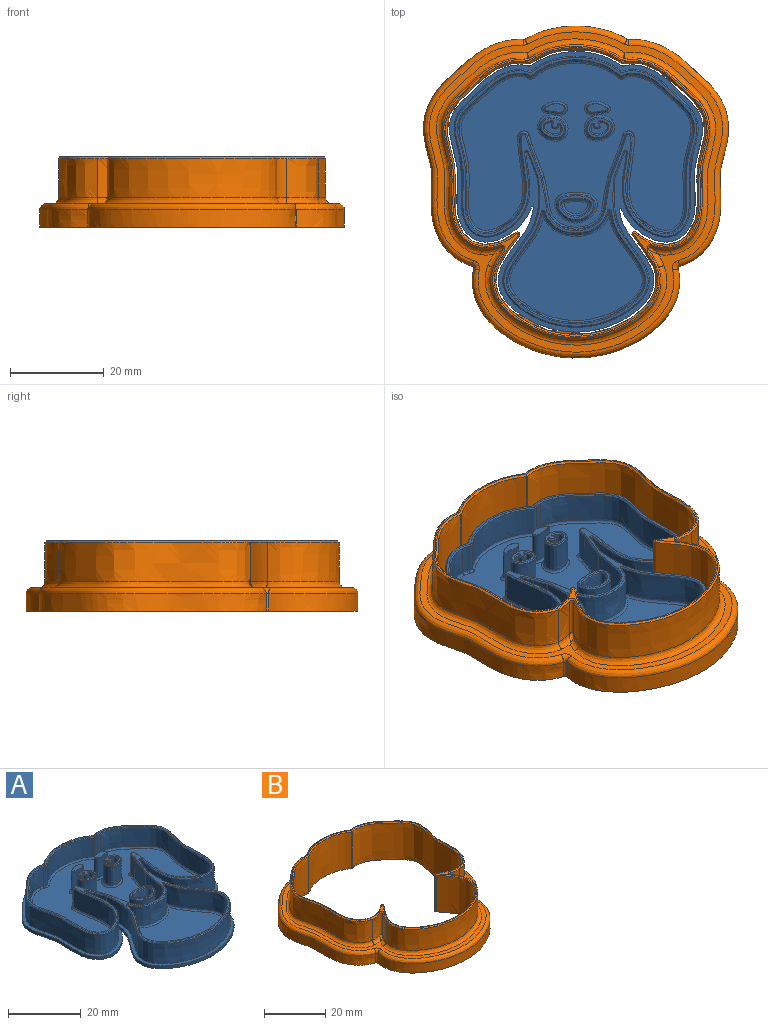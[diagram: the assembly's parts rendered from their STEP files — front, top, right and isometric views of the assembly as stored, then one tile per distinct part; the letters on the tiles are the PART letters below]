
ASSEMBLY  parts=2 mates=1
PART A: 147 faces, bbox 54.5x60.3x8.3 mm
  f0: plane 49.17x35.73mm, normal (0,0,1), area 1118mm2, adj f67,f68,f69,f70,f71,f72,f73,f74
  f1: plane 59.99x54.17mm, normal (0,0,1), area 259.7mm2, adj f2,f3,f4,f5,f20,f21,f22,f23
  f2: extruded ~37.82x17.38mm, area 63.9mm2, adj f1,f6,f57,f65
  f3: extruded ~19.16x2.96mm, area 20.4mm2, adj f1,f6,f65,f66
  f4: extruded ~37.76x17.54mm, area 64.3mm2, adj f1,f6,f58,f66
  f5: extruded ~33.25x26.68mm, area 78.1mm2, adj f1,f6,f57,f58
  f6: plane 59.99x54.17mm, normal (0,0,-1), area 2381.7mm2, adj f2,f3,f4,f5,f57,f58,f65,f66
  f7: extruded ~29.22x23.78mm, area 440.3mm2, adj f54,f55,f85,f133
  f8: extruded ~33.83x14.11mm, area 427.3mm2, adj f9,f59,f68,f115
  f9: extruded ~6.25x1.16mm, area 7.4mm2, adj f8,f10,f67,f116
  f10: extruded ~6.25x0.46mm, area 3.1mm2, adj f9,f61,f69,f118
  f11: extruded ~18.37x6.25mm, area 124.2mm2, adj f61,f62,f73,f122
  f12: extruded ~6.25x0.46mm, area 3.1mm2, adj f13,f62,f77,f126
  f13: extruded ~6.25x1.16mm, area 7.4mm2, adj f12,f14,f79,f128
  f14: extruded ~33.83x14.11mm, area 427.3mm2, adj f13,f64,f81,f130
  f15: extruded ~6.25x1.84mm, area 12mm2, adj f16,f64,f80,f127
  f16: extruded ~7.02x6.25mm, area 46.9mm2, adj f15,f17,f78,f125
  f17: extruded ~14.57x11.1mm, area 187.2mm2, adj f16,f18,f76,f123
  f18: extruded ~7.02x6.25mm, area 46.9mm2, adj f17,f19,f74,f121
  f19: extruded ~6.25x1.84mm, area 12mm2, adj f18,f59,f72,f119
  f20: extruded ~6.75x0.7mm, area 4.9mm2, adj f1,f21,f60,f106
  f21: extruded ~35.76x16.11mm, area 476.3mm2, adj f1,f20,f53,f104
  f22: extruded ~6.75x2.42mm, area 17.6mm2, adj f1,f23,f53,f100
  f23: extruded ~6.75x3.13mm, area 22.5mm2, adj f1,f22,f24,f99
  f24: extruded ~31.88x31.3mm, area 595mm2, adj f1,f23,f25,f101
  f25: extruded ~6.75x3.1mm, area 22.3mm2, adj f1,f24,f26,f103
  f26: extruded ~6.75x2.43mm, area 17.6mm2, adj f1,f25,f56,f105
  f27: extruded ~35.76x16.11mm, area 476.4mm2, adj f1,f28,f56,f109
  f28: extruded ~6.75x0.7mm, area 4.9mm2, adj f1,f27,f63,f111
  f29: extruded ~6.75x0.51mm, area 4.3mm2, adj f1,f30,f63,f114
  f30: extruded ~17.72x6.75mm, area 127mm2, adj f1,f29,f31,f112
  f31: extruded ~6.75x0.51mm, area 4.3mm2, adj f1,f30,f60,f110
  f32: extruded ~13.77x6.25mm, area 113mm2, adj f54,f55,f84,f132
  f33: plane 57.77x52.07mm, normal (0,0,1), area 101.2mm2, adj f99,f100,f101,f102,f103,f104,f105,f106
  f34: plane 28.32x22.06mm, normal (0,0,1), area 426.1mm2, adj f84,f85
  f35: extruded ~6.25x6.1mm, area 98.1mm2, adj f92,f98
  f36: extruded ~8.06x6.25mm, area 137.2mm2, adj f91,f97
  f37: plane 8.01x5.38mm, normal (0,0,1), area 9.6mm2, adj f97,f98
  f38: plane 5.13x2.56mm, normal (0,0,1), area 10mm2, adj f92
  f39: cylinder r=0.8mm len=6.75mm, axis (0,0,-1), area 21.2mm2, adj f43,f93,f94,f136
  f40: extruded ~6.75x3.54mm, area 54.2mm2, adj f43,f93,f94,f137
  f41: extruded ~6.25x5.54mm, area 100.7mm2, adj f90,f139
  f42: plane 5.29x4.35mm, normal (0,0,1), area 7.9mm2, adj f135,f136,f137,f138,f139
  f43: plane 3.66x2.67mm, normal (0,0,1), area 5.4mm2, adj f39,f40,f93,f94
  f44: extruded ~6.75x3.54mm, area 54.2mm2, adj f48,f95,f96,f142
  f45: extruded ~6.25x5.54mm, area 100.7mm2, adj f89,f144
  f46: cylinder r=0.8mm len=6.75mm, axis (0,0,-1), area 21.2mm2, adj f48,f95,f96,f141
  f47: plane 5.3x4.36mm, normal (0,0,1), area 8mm2, adj f140,f141,f142,f143,f144
  f48: plane 3.66x2.67mm, normal (0,0,1), area 5.4mm2, adj f44,f46,f95,f96
  f49: extruded ~6.4x4.57mm, area 68.2mm2, adj f88,f145
  f50: plane 4.48x1.88mm, normal (0,0,1), area 5.7mm2, adj f145
  f51: extruded ~6.4x4.57mm, area 68.2mm2, adj f87,f146
  f52: plane 4.49x1.9mm, normal (0,0,1), area 5.6mm2, adj f146
  f53: cylinder r=0.2mm len=6.75mm, axis (0,0,-1), area 3.9mm2, adj f1,f21,f22,f102
  f54: cylinder r=0.2mm len=6.25mm, axis (0,0,-1), area 3.4mm2, adj f7,f32,f86,f131
  f55: cylinder r=0.2mm len=6.25mm, axis (0,0,-1), area 3.4mm2, adj f7,f32,f83,f134
  f56: cylinder r=0.2mm len=6.75mm, axis (0,0,-1), area 3.9mm2, adj f1,f26,f27,f107
  f57: cylinder r=0.2mm len=1mm, axis (0,0,-1), area 0.6mm2, adj f1,f2,f5,f6
  f58: cylinder r=0.2mm len=1mm, axis (0,0,-1), area 0.6mm2, adj f1,f4,f5,f6
  f59: cylinder r=0.75mm len=6.25mm, axis (0,0,-1), area 13.4mm2, adj f8,f19,f70,f117
  f60: cylinder r=0.75mm len=6.75mm, axis (0,0,-1), area 5.2mm2, adj f1,f20,f31,f108
  f61: cylinder r=0.75mm len=6.25mm, axis (0,0,-1), area 5.8mm2, adj f10,f11,f71,f120
  f62: cylinder r=0.75mm len=6.25mm, axis (0,0,-1), area 5.8mm2, adj f11,f12,f75,f124
  f63: cylinder r=0.75mm len=6.75mm, axis (0,0,-1), area 5.2mm2, adj f1,f28,f29,f113
  f64: cylinder r=0.75mm len=6.25mm, axis (0,0,-1), area 13.5mm2, adj f14,f15,f82,f129
  f65: cylinder r=0.75mm len=1mm, axis (0,0,-1), area 0.7mm2, adj f1,f2,f3,f6
  f66: cylinder r=0.75mm len=1mm, axis (0,0,-1), area 0.7mm2, adj f1,f3,f4,f6
  f67: bspline ~1.47x0.77mm, area 0.9mm2, adj f0,f9,f68,f69
  f68: bspline ~33.87x24.37mm, area 53.1mm2, adj f0,f8,f67,f70
  f69: bspline ~0.91x0.78mm, area 0.4mm2, adj f0,f10,f67,f71
  f70: torus R=1.25mm, axis (0,0,1), area 2.1mm2, adj f0,f59,f68,f72
  f71: torus R=1.25mm, axis (0,0,1), area 0.9mm2, adj f0,f61,f69,f73
  f72: bspline ~3.24x1.36mm, area 1.5mm2, adj f0,f19,f70,f74
  f73: bspline ~19x4.03mm, area 15.4mm2, adj f0,f11,f71,f75
  f74: bspline ~10.3x4.11mm, area 5.9mm2, adj f0,f18,f72,f76
  f75: torus R=1.25mm, axis (0,0,1), area 0.9mm2, adj f0,f62,f73,f77
  f76: bspline ~17.48x16.85mm, area 23.1mm2, adj f0,f17,f74,f78
  f77: bspline ~0.89x0.74mm, area 0.4mm2, adj f0,f12,f75,f79
  f78: bspline ~10.33x4.12mm, area 5.9mm2, adj f0,f16,f76,f80
  f79: bspline ~1.64x0.78mm, area 0.9mm2, adj f0,f13,f77,f81
  f80: bspline ~3.26x1.37mm, area 1.5mm2, adj f0,f15,f78,f82
  f81: bspline ~33.88x14.21mm, area 53.1mm2, adj f0,f14,f79,f82
  f82: torus R=1.25mm, axis (0,0,1), area 2.1mm2, adj f0,f64,f80,f81
  f83: bspline ~2.25x0.67mm, area 0.3mm2, adj f55,f84,f85
  f84: bspline ~15.03x5.89mm, area 13.7mm2, adj f32,f34,f83,f86
  f85: bspline ~29.33x24.78mm, area 53.9mm2, adj f7,f34,f83,f86
  f86: bspline ~1.96x0.65mm, area 0.3mm2, adj f54,f84,f85
  f87: bspline ~5.58x2.99mm, area 9.3mm2, adj f0,f51
  f88: bspline ~5.58x2.99mm, area 9.3mm2, adj f0,f49
  f89: bspline ~6.55x5.6mm, area 13.6mm2, adj f0,f45
  f90: bspline ~6.55x5.59mm, area 13.5mm2, adj f0,f41
  f91: bspline ~9.13x6.56mm, area 18.2mm2, adj f0,f36
  f92: bspline ~6.13x3.56mm, area 11.3mm2, adj f35,f38
  f93: cylinder r=0.1mm len=6.75mm, axis (0,0,-1), area 1.7mm2, adj f39,f40,f43,f135
  f94: cylinder r=0.1mm len=6.75mm, axis (0,0,-1), area 1.6mm2, adj f39,f40,f43,f138
  f95: cylinder r=0.1mm len=6.75mm, axis (0,0,-1), area 1.6mm2, adj f44,f46,f48,f140
  f96: cylinder r=0.1mm len=6.75mm, axis (0,0,-1), area 1.7mm2, adj f44,f46,f48,f143
  f97: bspline ~8.11x5.55mm, area 7.5mm2, adj f36,f37
  f98: bspline ~6.62x4.05mm, area 5.8mm2, adj f35,f37
  f99: bspline ~3.41x1.44mm, area 1.2mm2, adj f23,f33,f100,f101
  f100: bspline ~2.51x1.19mm, area 0.9mm2, adj f22,f33,f99,f102
  f101: bspline ~36.19x31.37mm, area 31mm2, adj f24,f33,f99,f103
  f102: cone r=0.45mm half-angle=45deg, axis (0,0,1), area 0.3mm2, adj f33,f53,f100,f104
  f103: bspline ~3.39x1.44mm, area 1.2mm2, adj f25,f33,f101,f105
  f104: bspline ~35.95x16.31mm, area 24.7mm2, adj f21,f33,f102,f106
  f105: bspline ~2.52x1.19mm, area 0.9mm2, adj f26,f33,f103,f107
  f106: bspline ~0.75x0.43mm, area 0.3mm2, adj f20,f33,f104,f108
  f107: cone r=0.45mm half-angle=45deg, axis (0,0,1), area 0.3mm2, adj f33,f56,f105,f109
  f108: cone r=1mm half-angle=45deg, axis (0,0,1), area 0.3mm2, adj f33,f60,f106,f110
  f109: bspline ~35.96x16.32mm, area 24.5mm2, adj f27,f33,f107,f111
  f110: bspline ~0.65x0.58mm, area 0.2mm2, adj f31,f33,f108,f112
  f111: bspline ~0.75x0.43mm, area 0.3mm2, adj f28,f33,f109,f113
  f112: bspline ~17.72x2.88mm, area 6.6mm2, adj f30,f33,f110,f114
  f113: cone r=1mm half-angle=45deg, axis (0,0,1), area 0.3mm2, adj f33,f63,f111,f114
  f114: bspline ~0.65x0.58mm, area 0.2mm2, adj f29,f33,f112,f113
  f115: bspline ~34.49x14.72mm, area 24.5mm2, adj f8,f33,f116,f117
  f116: bspline ~1.24x0.47mm, area 0.4mm2, adj f9,f33,f115,f118
  f117: cone r=0.5mm half-angle=45deg, axis (0,0,-1), area 0.6mm2, adj f33,f59,f115,f119
  f118: bspline ~0.58x0.44mm, area 0.2mm2, adj f10,f33,f116,f120
  f119: bspline ~1.92x0.78mm, area 0.7mm2, adj f19,f33,f117,f121
  f120: cone r=0.5mm half-angle=45deg, axis (0,0,-1), area 0.3mm2, adj f33,f61,f118,f122
  f121: bspline ~7.09x2.87mm, area 2.6mm2, adj f18,f33,f119,f123
  f122: bspline ~18.7x3.45mm, area 7.1mm2, adj f11,f33,f120,f124
  f123: bspline ~15.05x11.35mm, area 10.7mm2, adj f17,f33,f121,f125
  f124: cone r=0.5mm half-angle=45deg, axis (0,0,-1), area 0.3mm2, adj f33,f62,f122,f126
  f125: bspline ~7.09x2.87mm, area 2.6mm2, adj f16,f33,f123,f127
  f126: bspline ~0.58x0.44mm, area 0.2mm2, adj f12,f33,f124,f128
  f127: bspline ~1.92x0.78mm, area 0.7mm2, adj f15,f33,f125,f129
  f128: bspline ~1.24x0.47mm, area 0.4mm2, adj f13,f33,f126,f130
  f129: cone r=0.5mm half-angle=45deg, axis (0,0,-1), area 0.6mm2, adj f33,f64,f127,f130
  f130: bspline ~34.46x14.72mm, area 24.4mm2, adj f14,f33,f128,f129
  f131: cone r=0.45mm half-angle=45deg, axis (0,0,1), area 0.3mm2, adj f33,f54,f132,f133
  f132: bspline ~13.77x4.92mm, area 6.3mm2, adj f32,f33,f131,f134
  f133: bspline ~29.91x24.07mm, area 25.1mm2, adj f7,f33,f131,f134
  f134: cone r=0.45mm half-angle=45deg, axis (0,0,1), area 0.3mm2, adj f33,f55,f132,f133
  f135: cone r=0.35mm half-angle=45deg, axis (0,0,1), area 0.2mm2, adj f42,f93,f136,f137
  f136: cone r=0.55mm half-angle=45deg, axis (0,0,-1), area 0.9mm2, adj f39,f42,f135,f138
  f137: bspline ~4.09x3.1mm, area 3.1mm2, adj f40,f42,f135,f138
  f138: cone r=0.35mm half-angle=45deg, axis (0,0,1), area 0.2mm2, adj f42,f94,f136,f137
  f139: bspline ~5.58x4.64mm, area 5.4mm2, adj f41,f42
  f140: cone r=0.35mm half-angle=45deg, axis (0,0,1), area 0.2mm2, adj f47,f95,f141,f142
  f141: cone r=0.55mm half-angle=45deg, axis (0,0,-1), area 0.9mm2, adj f46,f47,f140,f143
  f142: bspline ~4.09x3.1mm, area 3.1mm2, adj f44,f47,f140,f143
  f143: cone r=0.35mm half-angle=45deg, axis (0,0,1), area 0.2mm2, adj f47,f96,f141,f142
  f144: bspline ~5.54x4.59mm, area 5.4mm2, adj f45,f47
  f145: bspline ~4.59x1.99mm, area 1.5mm2, adj f49,f50
  f146: bspline ~4.59x2.01mm, area 1.5mm2, adj f51,f52
PART B: 85 faces, bbox 65.6x71.4x15.5 mm
  f0: extruded ~40.8x18.2mm, area 461.4mm2, adj f1,f33,f56,f83
  f1: extruded ~8.4x3.99mm, area 34.1mm2, adj f0,f37,f58,f81
  f2: extruded ~8.4x3.68mm, area 35.4mm2, adj f3,f37,f62,f77
  f3: extruded ~36.25x15.36mm, area 453.4mm2, adj f2,f4,f64,f75
  f4: extruded ~8.4x3.67mm, area 35.2mm2, adj f3,f35,f63,f73
  f5: extruded ~8.4x3.98mm, area 33.9mm2, adj f6,f35,f59,f76
  f6: extruded ~40.8x18.2mm, area 461.2mm2, adj f5,f34,f57,f78
  f7: extruded ~20.01x8.4mm, area 177.7mm2, adj f33,f34,f53,f82
  f8: extruded ~14.65x6.78mm, area 108.4mm2, adj f9,f21,f23,f40
  f9: extruded ~38.85x17.49mm, area 771.2mm2, adj f8,f10,f23,f39
  f10: cylinder r=0.25mm len=14.68mm, axis (0,0,-1), area 3.3mm2, adj f9,f11,f23,f39,f52
  f11: extruded ~19.75x14.65mm, area 308mm2, adj f10,f12,f23,f52
  f12: cylinder r=0.25mm len=14.68mm, axis (0,0,-1), area 3.3mm2, adj f11,f13,f23,f44,f52
  f13: extruded ~38.85x17.49mm, area 770.9mm2, adj f12,f14,f23,f44
  f14: extruded ~14.65x6.74mm, area 107.7mm2, adj f13,f15,f23,f46
  f15: extruded ~14.65x0.05mm, area 1mm2, adj f14,f23,f36,f48
  f16: extruded ~14.65x0.06mm, area 1mm2, adj f17,f23,f36,f51
  f17: extruded ~14.65x6.53mm, area 115.1mm2, adj f16,f18,f23,f49
  f18: extruded ~34.32x14.65mm, area 751mm2, adj f17,f19,f23,f47
  f19: extruded ~14.65x6.57mm, area 116mm2, adj f18,f20,f23,f45
  f20: extruded ~14.65x0.06mm, area 1mm2, adj f19,f23,f38,f43
  f21: extruded ~14.65x0.05mm, area 1mm2, adj f8,f23,f38,f41
  f22: plane 62.73x57.15mm, normal (0,0,1), area 66.1mm2, adj f39,f40,f41,f42,f43,f44,f45,f46
  f23: plane 70.98x65.17mm, normal (0,0,-1), area 1058.9mm2, adj f8,f9,f10,f11,f12,f13,f14,f15
  f24: extruded ~44.32x19.07mm, area 246.8mm2, adj f23,f29,f30,f67
  f25: extruded ~48.44x21.35mm, area 242.1mm2, adj f23,f29,f32,f71
  f26: extruded ~21.92x3.75mm, area 85.8mm2, adj f23,f31,f32,f70
  f27: extruded ~48.44x21.35mm, area 242.1mm2, adj f23,f30,f31,f66
  f28: plane 68.48x62.69mm, normal (0,0,1), area 317.4mm2, adj f65,f66,f67,f68,f69,f70,f71,f72
  f29: cylinder r=0.5mm len=3.75mm, axis (0,0,-1), area 2.8mm2, adj f23,f24,f25,f69
  f30: cylinder r=0.5mm len=3.75mm, axis (0,0,-1), area 2.8mm2, adj f23,f24,f27,f65
  f31: cylinder r=0.5mm len=3.75mm, axis (0,0,-1), area 1.1mm2, adj f23,f26,f27,f68
  f32: cylinder r=0.5mm len=3.75mm, axis (0,0,-1), area 1.1mm2, adj f23,f25,f26,f72
  f33: cylinder r=0.5mm len=8.4mm, axis (0,0,-1), area 3.3mm2, adj f0,f7,f54,f84
  f34: cylinder r=0.5mm len=8.4mm, axis (0,0,-1), area 3.3mm2, adj f6,f7,f55,f80
  f35: cylinder r=0.5mm len=8.4mm, axis (0,0,-1), area 10.5mm2, adj f4,f5,f61,f74
  f36: cylinder r=0.5mm len=14.65mm, axis (0,0,-1), area 21mm2, adj f15,f16,f23,f50
  f37: cylinder r=0.5mm len=8.4mm, axis (0,0,-1), area 10.6mm2, adj f1,f2,f60,f79
  f38: cylinder r=0.5mm len=14.65mm, axis (0,0,-1), area 21mm2, adj f20,f21,f23,f42
  f39: bspline ~39.56x18.67mm, area 26.3mm2, adj f9,f10,f22,f40,f52
  f40: bspline ~7.02x2.98mm, area 3.7mm2, adj f8,f22,f39,f41
  f41: bspline ~0.35x0.32mm, area 0mm2, adj f21,f22,f40,f42
  f42: cone r=0.15mm half-angle=45deg, axis (0,0,-1), area 0.5mm2, adj f22,f38,f41,f43
  f43: bspline ~0.35x0.33mm, area 0mm2, adj f20,f22,f42,f45
  f44: bspline ~39.56x18.67mm, area 26.3mm2, adj f12,f13,f22,f46,f52
  f45: bspline ~6.77x4.7mm, area 3.9mm2, adj f19,f22,f43,f47
  f46: bspline ~6.98x2.99mm, area 3.7mm2, adj f14,f22,f44,f48
  f47: bspline ~35.03x15.05mm, area 25.7mm2, adj f18,f22,f45,f49
  f48: bspline ~0.35x0.32mm, area 0mm2, adj f15,f22,f46,f50
  f49: bspline ~6.73x4.66mm, area 3.9mm2, adj f17,f22,f47,f51
  f50: cone r=0.15mm half-angle=45deg, axis (0,0,-1), area 0.5mm2, adj f22,f36,f48,f51
  f51: bspline ~0.35x0.32mm, area 0mm2, adj f16,f22,f49,f50
  f52: bspline ~21.91x4.05mm, area 10.5mm2, adj f10,f11,f12,f22,f39,f44
  f53: bspline ~20.01x3.22mm, area 10.4mm2, adj f7,f22,f54,f55
  f54: cone r=0.85mm half-angle=45deg, axis (0,0,1), area 0.3mm2, adj f22,f33,f53,f56
  f55: cone r=0.85mm half-angle=45deg, axis (0,0,1), area 0.3mm2, adj f22,f34,f53,f57
  f56: bspline ~40.88x18.28mm, area 27.1mm2, adj f0,f22,f54,f58
  f57: bspline ~40.87x18.27mm, area 26.8mm2, adj f6,f22,f55,f59
  f58: bspline ~3.99x0.99mm, area 2mm2, adj f1,f22,f56,f60
  f59: bspline ~3.98x0.98mm, area 2mm2, adj f5,f22,f57,f61
  f60: cone r=0.85mm half-angle=45deg, axis (0,0,1), area 0.8mm2, adj f22,f37,f58,f62
  f61: cone r=0.85mm half-angle=45deg, axis (0,0,1), area 0.8mm2, adj f22,f35,f59,f63
  f62: bspline ~3.8x2.3mm, area 2.1mm2, adj f2,f22,f60,f64
  f63: bspline ~3.79x2.28mm, area 2.1mm2, adj f4,f22,f61,f64
  f64: bspline ~36.41x15.36mm, area 26.4mm2, adj f3,f22,f62,f63
  f65: torus R=1.75mm, axis (0,0,-1), area 2.8mm2, adj f28,f30,f66,f67
  f66: bspline ~48.61x21.9mm, area 123.9mm2, adj f27,f28,f65,f68
  f67: bspline ~44.36x19.54mm, area 126.1mm2, adj f24,f28,f65,f69
  f68: torus R=1.75mm, axis (0,0,-1), area 1.1mm2, adj f28,f31,f66,f70
  f69: torus R=1.75mm, axis (0,0,-1), area 2.8mm2, adj f28,f29,f67,f71
  f70: bspline ~23.29x4.3mm, area 44mm2, adj f26,f28,f68,f72
  f71: bspline ~48.61x21.91mm, area 123.9mm2, adj f25,f28,f69,f72
  f72: torus R=1.75mm, axis (0,0,-1), area 1.1mm2, adj f28,f32,f70,f71
  f73: bspline ~13.95x6.68mm, area 6.6mm2, adj f4,f28,f74,f75
  f74: bspline ~2.93x2.16mm, area 2mm2, adj f35,f73,f76
  f75: bspline ~38.85x24.82mm, area 109.3mm2, adj f3,f28,f73,f77
  f76: bspline ~7.12x2mm, area 6.5mm2, adj f5,f28,f74,f78
  f77: bspline ~14.01x6.76mm, area 6.6mm2, adj f2,f28,f75,f79
  f78: bspline ~45.77x28.35mm, area 110.1mm2, adj f6,f28,f76,f80
  f79: bspline ~2.95x2.17mm, area 1.5mm2, adj f37,f77,f81
  f80: bspline ~1.53x1.32mm, area 0.3mm2, adj f34,f78,f82
  f81: bspline ~7.05x1.99mm, area 6.5mm2, adj f1,f28,f79,f83
  f82: bspline ~22.12x4.46mm, area 42mm2, adj f7,f28,f80,f84
  f83: bspline ~45.72x28.34mm, area 110.2mm2, adj f0,f28,f81,f84
  f84: bspline ~1.53x1.32mm, area 0.3mm2, adj f33,f82,f83
PLACE A t=(-12.64,-14.1,-1.03)mm
PLACE B t=(-12.64,-14.14,-1.03)mm
MATE fastened A.f6 <-> B.f23  axis (0,0,-1) through (-12.64,0.93,-1.03)mm
